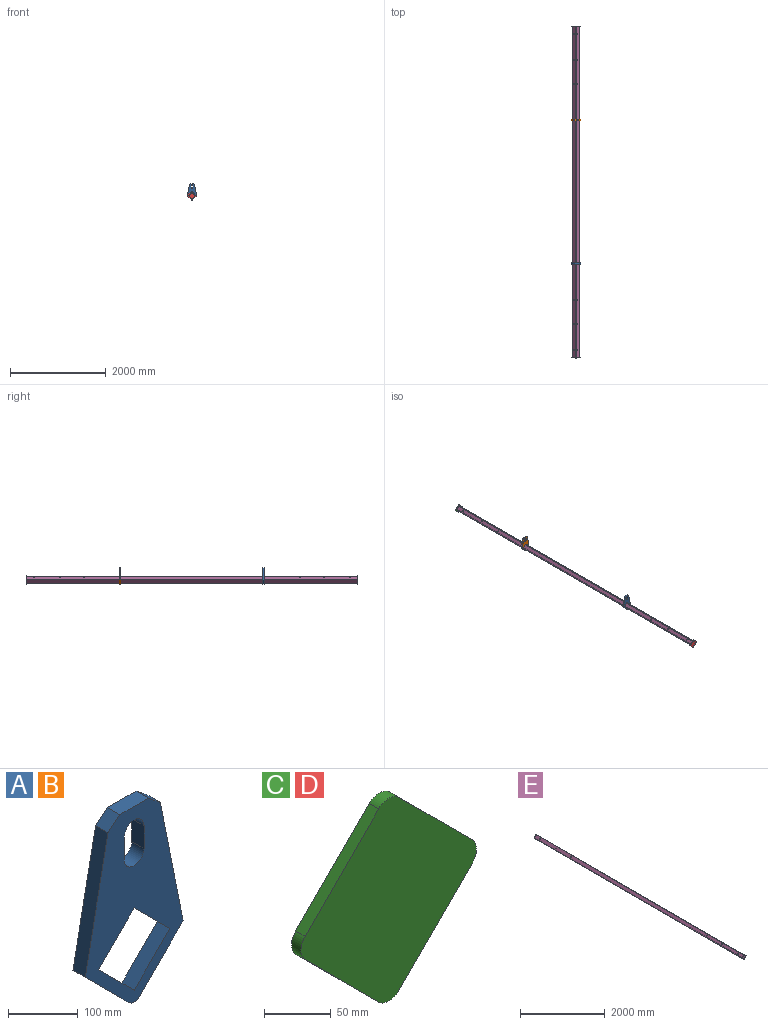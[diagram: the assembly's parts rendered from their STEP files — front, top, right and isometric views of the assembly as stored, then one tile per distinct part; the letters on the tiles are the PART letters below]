
ASSEMBLY  parts=5 mates=4
PART A: 18 faces, bbox 198x25x342.8 mm
  f0: plane 72.13x72.13mm, normal (-0.71,0,-0.71), area 2550mm2, adj f1,f15,f16,f17
  f1: plane 72.13x72.13mm, normal (-0.71,0,0.71), area 2550mm2, adj f0,f2,f16,f17
  f2: plane 72.13x72.13mm, normal (0.71,0,0.71), area 2550mm2, adj f1,f15,f16,f17
  f3: plane 25x23.92mm, normal (-0.63,0,0.77), area 773.3mm2, adj f4,f13,f16,f17
  f4: plane 230.39x46.08mm, normal (-0.98,0,0.2), area 5873.8mm2, adj f3,f5,f16,f17
  f5: plane 88.39x88.39mm, normal (-0.71,0,-0.71), area 3125mm2, adj f4,f6,f16,f17
  f6: cylinder r=15mm len=25mm, axis (0,1,0), area 589mm2, adj f5,f7,f16,f17
  f7: plane 88.39x88.39mm, normal (0.71,0,-0.71), area 3125mm2, adj f6,f8,f16,f17
  f8: plane 230.39x46.08mm, normal (0.98,0,0.2), area 5873.8mm2, adj f7,f9,f16,f17
  f9: plane 25x23.92mm, normal (0.63,0,0.77), area 773.3mm2, adj f8,f13,f16,f17
  f10: plane 40x25mm, normal (-1,0,0), area 1000mm2, adj f11,f14,f16,f17
  f11: cylinder r=20mm len=40mm, axis (0,1,0), area 1570.8mm2, adj f10,f12,f16,f17
  f12: plane 40x25mm, normal (1,0,0), area 1000mm2, adj f11,f14,f16,f17
  f13: plane 57.99x25mm, normal (0,0,1), area 1449.7mm2, adj f3,f9,f16,f17
  f14: cylinder r=20mm len=40mm, axis (0,1,0), area 1570.8mm2, adj f10,f12,f16,f17
  f15: plane 72.13x72.13mm, normal (0.71,0,-0.71), area 2550mm2, adj f0,f2,f16,f17
  f16: plane 342.78x197.99mm, normal (0,-1,0), area 33096.3mm2, adj f0,f1,f2,f3,f4,f5,f6,f7
  f17: plane 342.78x197.99mm, normal (0,1,0), area 33096.3mm2, adj f0,f1,f2,f3,f4,f5,f6,f7
PART B: same geometry as A
PART C: 10 faces, bbox 185.6x10x185.6 mm
  f0: plane 77.78x77.78mm, normal (0.71,0,-0.71), area 1100mm2, adj f1,f7,f8,f9
  f1: cylinder r=15mm len=21.21mm, axis (0,1,0), area 235.6mm2, adj f0,f2,f8,f9
  f2: plane 77.78x77.78mm, normal (0.71,0,0.71), area 1100mm2, adj f1,f3,f8,f9
  f3: cylinder r=15mm len=21.21mm, axis (0,1,0), area 235.6mm2, adj f2,f4,f8,f9
  f4: plane 77.78x77.78mm, normal (-0.71,0,0.71), area 1100mm2, adj f3,f5,f8,f9
  f5: cylinder r=15mm len=21.21mm, axis (0,1,0), area 235.6mm2, adj f4,f6,f8,f9
  f6: plane 77.78x77.78mm, normal (-0.71,0,-0.71), area 1100mm2, adj f5,f7,f8,f9
  f7: cylinder r=15mm len=21.21mm, axis (0,1,0), area 235.6mm2, adj f0,f6,f8,f9
  f8: plane 185.56x185.56mm, normal (0,-1,0), area 19406.9mm2, adj f0,f1,f2,f3,f4,f5,f6,f7
  f9: plane 185.56x185.56mm, normal (0,1,0), area 19406.9mm2, adj f0,f1,f2,f3,f4,f5,f6,f7
PART D: same geometry as C
PART E: 30 faces, bbox 138.3x6920x138.3 mm
  f0: plane 6920x65.42mm, normal (0.71,0,-0.71), area 640238.4mm2, adj f1,f15,f16,f17
  f1: cylinder r=3.74mm len=6920mm, axis (0,1,0), area 40653.5mm2, adj f0,f2,f16,f17
  f2: plane 6920x65.42mm, normal (0.71,0,0.71), area 638353.5mm2, adj f1,f3,f16,f17,f18,f19,f20,f21
  f3: cylinder r=3.74mm len=6920mm, axis (0,1,0), area 40653.5mm2, adj f2,f4,f16,f17
  f4: plane 6920x65.42mm, normal (-0.71,0,0.71), area 638353.5mm2, adj f3,f5,f16,f17,f24,f25,f26,f27
  f5: cylinder r=3.74mm len=6920mm, axis (0,1,0), area 40653.5mm2, adj f4,f6,f16,f17
  f6: plane 6920x65.42mm, normal (-0.71,0,-0.71), area 640238.4mm2, adj f5,f15,f16,f17
  f7: cylinder r=3.74mm len=6920mm, axis (0,1,0), area 40653.5mm2, adj f8,f14,f16,f17
  f8: plane 6920x54.11mm, normal (-0.71,0,0.71), area 529518.4mm2, adj f7,f9,f16,f17
  f9: cylinder r=3.74mm len=6920mm, axis (0,1,0), area 40653.5mm2, adj f8,f10,f16,f17
  f10: plane 6920x54.11mm, normal (0.71,0,0.71), area 529518.4mm2, adj f9,f11,f16,f17
  f11: cylinder r=3.74mm len=6920mm, axis (0,1,0), area 40653.5mm2, adj f10,f12,f16,f17
  f12: plane 6920x54.11mm, normal (0.71,0,-0.71), area 527633.4mm2, adj f11,f13,f16,f17,f24,f25,f26,f27
  f13: cylinder r=3.74mm len=6920mm, axis (0,1,0), area 40653.5mm2, adj f12,f14,f16,f17
  f14: plane 6920x54.11mm, normal (-0.71,0,-0.71), area 527633.4mm2, adj f7,f13,f16,f17,f18,f19,f20,f21
  f15: cylinder r=3.74mm len=6920mm, axis (0,1,0), area 40653.5mm2, adj f0,f6,f16,f17
  f16: plane 138.32x138.32mm, normal (0,-1,0), area 2944mm2, adj f0,f1,f2,f3,f4,f5,f6,f7
  f17: plane 138.32x138.32mm, normal (0,1,0), area 2944mm2, adj f0,f1,f2,f3,f4,f5,f6,f7
  f18: cylinder r=10mm len=20mm, axis (0.71,0,0.71), area 502.7mm2, adj f2,f14
  f19: cylinder r=10mm len=20mm, axis (0.71,0,0.71), area 502.7mm2, adj f2,f14
  f20: cylinder r=10mm len=20mm, axis (0.71,0,0.71), area 502.7mm2, adj f2,f14
  f21: cylinder r=10mm len=20mm, axis (0.71,0,0.71), area 502.7mm2, adj f2,f14
  f22: cylinder r=10mm len=20mm, axis (0.71,0,0.71), area 502.7mm2, adj f2,f14
  f23: cylinder r=10mm len=20mm, axis (0.71,0,0.71), area 502.7mm2, adj f2,f14
  f24: cylinder r=10mm len=20mm, axis (-0.71,0,0.71), area 502.7mm2, adj f4,f12
  f25: cylinder r=10mm len=20mm, axis (-0.71,0,0.71), area 502.7mm2, adj f4,f12
  f26: cylinder r=10mm len=20mm, axis (-0.71,0,0.71), area 502.7mm2, adj f4,f12
  f27: cylinder r=10mm len=20mm, axis (-0.71,0,0.71), area 502.7mm2, adj f4,f12
  f28: cylinder r=10mm len=20mm, axis (-0.71,0,0.71), area 502.7mm2, adj f4,f12
  f29: cylinder r=10mm len=20mm, axis (-0.71,0,0.71), area 502.7mm2, adj f4,f12
PLACE A t=(-669.95,-1778.17,135.1)mm
PLACE B rot(axis=(0,0,1),180deg) t=(-669.95,1197.33,135.1)mm
PLACE C t=(-670.66,3173.33,135.81)mm
PLACE D t=(-670.66,-3756.67,135.81)mm
PLACE E t=(-670.66,-296.67,135.81)mm
MATE fastened B.f0 <-> E.f4  axis (0.71,0,-0.71) through (-706.02,1197.33,171.16)mm
MATE fastened C.f8 <-> E.f17  axis (0,-1,0) through (-670.66,3163.33,135.81)mm
MATE fastened D.f9 <-> E.f16  axis (0,1,0) through (-670.66,-3756.67,135.81)mm
MATE fastened A.f15 <-> E.f4  axis (0.71,0,-0.71) through (-706.02,-1790.67,171.16)mm
